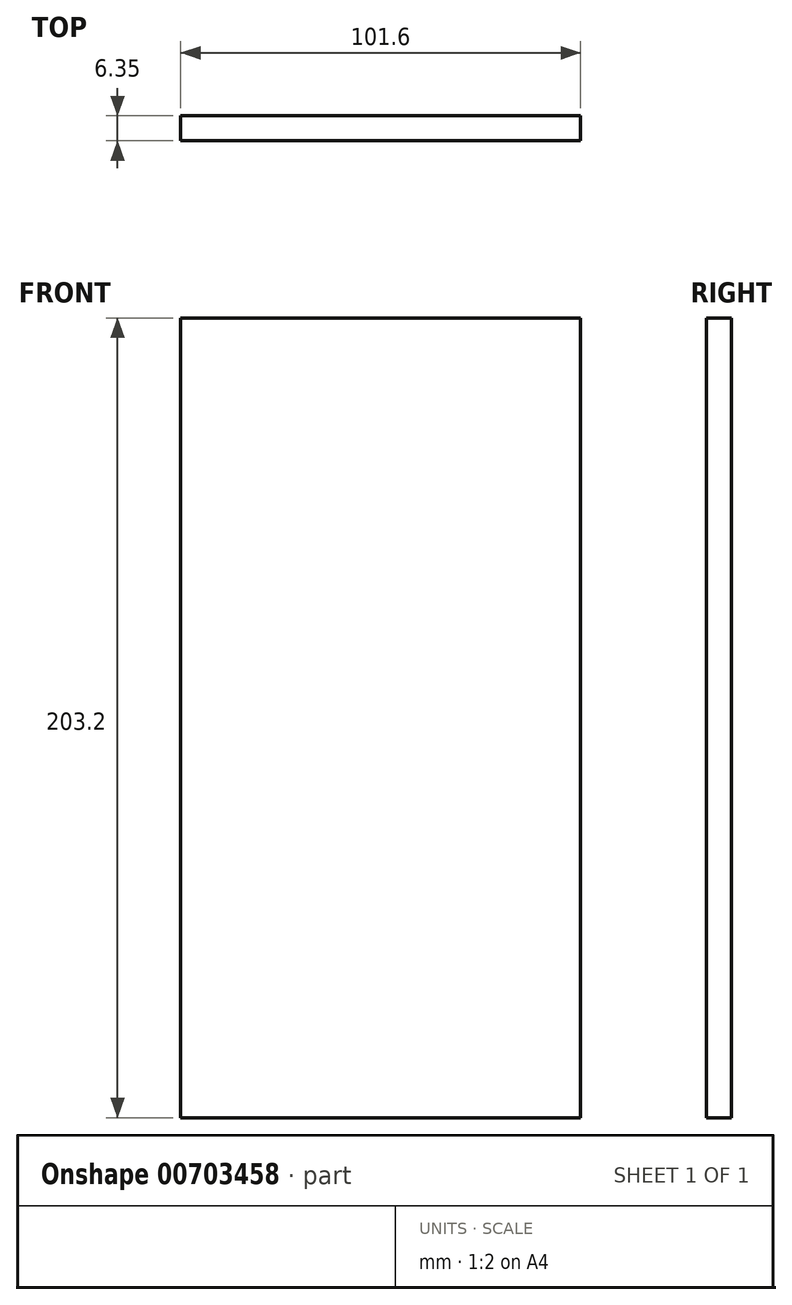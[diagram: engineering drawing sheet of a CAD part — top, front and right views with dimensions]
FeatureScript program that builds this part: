
annotation { "Feature Type Name" : "Feature", "Feature Type Description" : "" }
export const myFeature = defineFeature(function(context is Context, id is Id, definition is map)
    precondition{}
    {
        {
            var Q0;
            Q0=qCreatedBy(makeId("Front.planeOp"),FACE);
            var sketch = newSketch(context, id + "F0", { "sketchPlane" : qUnion([Q0])});
            skLineSegment(sketch, "E0.bottom", {"start": v(-50.8, 101.6) * mm, "end": v(50.8, 101.6) * mm});
            skLineSegment(sketch, "E0.top", {"start": v(-50.8, -101.6) * mm, "end": v(50.8, -101.6) * mm});
            skLineSegment(sketch, "E0.left", {"start": v(-50.8, 101.6) * mm, "end": v(-50.8, -101.6) * mm});
            skLineSegment(sketch, "E0.right", {"start": v(50.8, 101.6) * mm, "end": v(50.8, -101.6) * mm});
            skPoint(sketch, "E0.middle", {"position": v(0, 0) * mm});
            skSolve(sketch);
        }
        {
            var Q0;
            Q0 = qSketchRegion(id + "F0", true);
            extrude(context, id + "F1", {"entities" : qUnion([Q0]), "depth" : 6.35 * mm, "offsetDistance" : 25.4 * mm});
        }
    });
